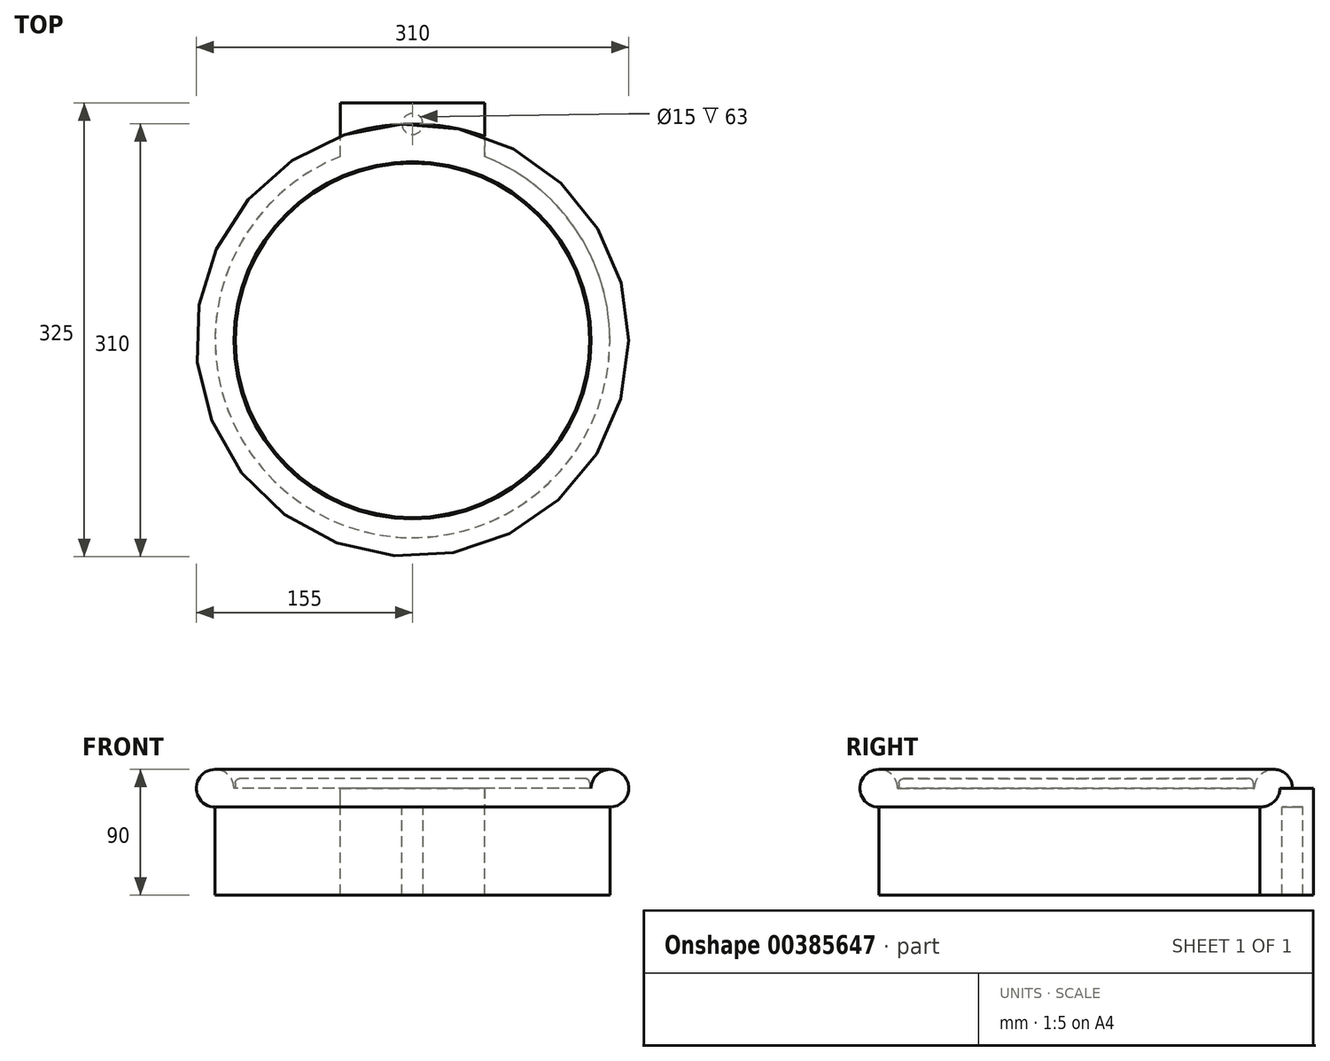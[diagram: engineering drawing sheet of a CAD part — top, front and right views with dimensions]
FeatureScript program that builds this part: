
annotation { "Feature Type Name" : "Feature", "Feature Type Description" : "" }
export const myFeature = defineFeature(function(context is Context, id is Id, definition is map)
    precondition{}
    {
        {
            var Q0;
            Q0=qCreatedBy(makeId("Top.planeOp"),FACE);
            var sketch = newSketch(context, id + "F0", { "sketchPlane" : qUnion([Q0])});
            skCircle(sketch, "E0", {"center": v(0, 0) * mm, "radius": 155 * mm});
            skCircle(sketch, "E1", {"center": v(0, 0) * mm, "radius": 141.5 * mm});
            skCircle(sketch, "E2", {"center": v(0, 0) * mm, "radius": 128 * mm});
            skCircle(sketch, "E3", {"center": v(0, 0) * mm, "radius": 127 * mm});
            skLineSegment(sketch, "E4.top", {"start": v(-51.67, 170) * mm, "end": v(51.67, 170) * mm});
            skLineSegment(sketch, "E4.left", {"start": v(-51.67, 131.73) * mm, "end": v(-51.67, 170) * mm});
            skLineSegment(sketch, "E4.right", {"start": v(51.67, 131.73) * mm, "end": v(51.67, 170) * mm});
            skLineSegment(sketch, "E5", {"start": v(0, 0) * mm, "end": v(0, -155) * mm, "construction": true});
            skLineSegment(sketch, "E6", {"start": v(0, -128) * mm, "end": v(0, -141.5) * mm, "construction": true});
            skLineSegment(sketch, "E7", {"start": v(-6.7, -141.5) * mm, "end": v(6.7, -141.5) * mm, "construction": true});
            skCircle(sketch, "E8", {"center": v(0, 155) * mm, "radius": 7.5 * mm});
            skSolve(sketch);
        }
        {
            assignVariable(context, id + "F1", {"name" : "raio", "anyValue" : 13.5});
        }
        {
            assignVariable(context, id + "F2", {"name" : "alt", "anyValue" : 90 - 2 * 13.5});
        }
        {
            var Q0;
            {var subQ5=sQuery(id+"F0.wireOp",EDGE,"E4.top");Q0=makeQuery(id+"F0.imprint","IMPRINT",FACE,{"disambiguationData":[TD([[makeQuery(id+"F0.imprint","IMPRINT",EDGE,{"derivedFrom":subQ5}),-1.0]])]});}
            var Q1;
            {var subQ0=sQuery(id+"F0.wireOp",EDGE,"E4.left");var subQ1=sQuery(id+"F0.wireOp",EDGE,"E0");var subQ2=makeQuery(id+"F0.imprint","INTERSECT",VERTEX,{"derivedFrom":[subQ1,subQ0]});Q1=makeQuery(id+"F0.imprint","IMPRINT",FACE,{"disambiguationData":[TD([[makeQuery(id+"F0.imprint","IMPRINT",EDGE,{"disambiguationData":[TD([[subQ2,1.0]])],"derivedFrom":subQ1}),1.0]])]});}
            var Q2;
            Q2=makeQuery(id+"F0.imprint","IMPRINT",FACE,{"disambiguationData":[TD([[makeQuery(id+"F0.imprint","IMPRINT",EDGE,{"derivedFrom":sQuery(id+"F0.wireOp",EDGE,"E2")}),-1.0]])]});
            var Q3;
            Q3=makeQuery(id+"F0.imprint","IMPRINT",FACE,{"disambiguationData":[TD([[makeQuery(id+"F0.imprint","IMPRINT",EDGE,{"derivedFrom":sQuery(id+"F0.wireOp",EDGE,"E2")}),1.0]])]});
            var Q4;
            Q4=makeQuery(id+"F0.imprint","IMPRINT",FACE,{"disambiguationData":[TD([[makeQuery(id+"F0.imprint","IMPRINT",EDGE,{"derivedFrom":sQuery(id+"F0.wireOp",EDGE,"E3")}),1.0]])]});
            extrude(context, id + "F3", {"entities" : qUnion([Q0, Q1, Q2, Q3, Q4]), "oppositeDirection" : true, "depth" : (getVariable(context, 'alt')) * mm});
        }
        {
            var Q0;
            {var subQ0=sQuery(id+"F0.wireOp",EDGE,"E4.left");var subQ1=sQuery(id+"F0.wireOp",EDGE,"E0");var subQ2=makeQuery(id+"F0.imprint","INTERSECT",VERTEX,{"derivedFrom":[subQ1,subQ0]});Q0=makeQuery(id+"F0.imprint","IMPRINT",FACE,{"disambiguationData":[TD([[makeQuery(id+"F0.imprint","IMPRINT",EDGE,{"disambiguationData":[TD([[subQ2,-1.0]])],"derivedFrom":subQ1}),1.0]])]});}
            var Q1;
            Q1=makeQuery(id+"F0.imprint","IMPRINT",FACE,{"disambiguationData":[TD([[makeQuery(id+"F0.imprint","IMPRINT",EDGE,{"derivedFrom":sQuery(id+"F0.wireOp",EDGE,"E2")}),-1.0]])]});
            var Q2;
            Q2=makeQuery(id+"F0.imprint","IMPRINT",FACE,{"disambiguationData":[TD([[makeQuery(id+"F0.imprint","IMPRINT",EDGE,{"derivedFrom":sQuery(id+"F0.wireOp",EDGE,"E2")}),1.0]])]});
            var Q3;
            Q3=makeQuery(id+"F0.imprint","IMPRINT",FACE,{"disambiguationData":[TD([[makeQuery(id+"F0.imprint","IMPRINT",EDGE,{"derivedFrom":sQuery(id+"F0.wireOp",EDGE,"E3")}),1.0]])]});
            var Q4;
            {var subQ0=sQuery(id+"F0.wireOp",EDGE,"E4.left");var subQ1=sQuery(id+"F0.wireOp",EDGE,"E0");var subQ2=makeQuery(id+"F0.imprint","INTERSECT",VERTEX,{"derivedFrom":[subQ1,subQ0]});Q4=makeQuery(id+"F0.imprint","IMPRINT",FACE,{"disambiguationData":[TD([[makeQuery(id+"F0.imprint","IMPRINT",EDGE,{"disambiguationData":[TD([[subQ2,1.0]])],"derivedFrom":subQ1}),1.0]])]});}
            var Q5;
            {var subQ5=sQuery(id+"F0.wireOp",EDGE,"E4.top");Q5=makeQuery(id+"F0.imprint","IMPRINT",FACE,{"disambiguationData":[TD([[makeQuery(id+"F0.imprint","IMPRINT",EDGE,{"derivedFrom":subQ5}),-1.0]])]});}
            var Q6;
            {var subQ0=sQuery(id+"F0.wireOp",EDGE,"E8");var subQ1=sQuery(id+"F0.wireOp",EDGE,"E0");var subQ2=makeQuery(id+"F0.imprint","INTERSECT",VERTEX,{"disambiguationData":[OD(0.0)],"derivedFrom":[subQ1,subQ0]});Q6=makeQuery(id+"F0.imprint","IMPRINT",FACE,{"disambiguationData":[TD([[makeQuery(id+"F0.imprint","IMPRINT",EDGE,{"disambiguationData":[TD([[subQ2,-1.0]])],"derivedFrom":subQ1}),1.0]])]});}
            var Q7;
            {var subQ0=sQuery(id+"F0.wireOp",EDGE,"E8");var subQ1=sQuery(id+"F0.wireOp",EDGE,"E0");var subQ2=makeQuery(id+"F0.imprint","INTERSECT",VERTEX,{"disambiguationData":[OD(0.0)],"derivedFrom":[subQ1,subQ0]});Q7=makeQuery(id+"F0.imprint","IMPRINT",FACE,{"disambiguationData":[TD([[makeQuery(id+"F0.imprint","IMPRINT",EDGE,{"disambiguationData":[TD([[subQ2,-1.0]])],"derivedFrom":subQ1}),-1.0]])]});}
            extrude(context, id + "F4", {"entities" : qUnion([Q0, Q1, Q2, Q3, Q4, Q5, Q6, Q7]), "operationType" : NewBodyOperationType.ADD, "depth" : (getVariable(context, 'raio')) * mm});
        }
        {
            var Q0;
            {var subQ0=sQuery(id+"F0.wireOp",EDGE,"E4.left");var subQ1=sQuery(id+"F0.wireOp",EDGE,"E0");var subQ2=makeQuery(id+"F0.imprint","INTERSECT",VERTEX,{"derivedFrom":[subQ1,subQ0]});Q0=makeQuery(id+"F0.imprint","IMPRINT",FACE,{"disambiguationData":[TD([[makeQuery(id+"F0.imprint","IMPRINT",EDGE,{"disambiguationData":[TD([[subQ2,-1.0]])],"derivedFrom":subQ1}),1.0]])]});}
            var Q1;
            Q1=makeQuery(id+"F0.imprint","IMPRINT",FACE,{"disambiguationData":[TD([[makeQuery(id+"F0.imprint","IMPRINT",EDGE,{"derivedFrom":sQuery(id+"F0.wireOp",EDGE,"E2")}),-1.0]])]});
            var Q2;
            {var subQ0=sQuery(id+"F0.wireOp",EDGE,"E4.left");var subQ1=sQuery(id+"F0.wireOp",EDGE,"E0");var subQ2=makeQuery(id+"F0.imprint","INTERSECT",VERTEX,{"derivedFrom":[subQ1,subQ0]});Q2=makeQuery(id+"F0.imprint","IMPRINT",FACE,{"disambiguationData":[TD([[makeQuery(id+"F0.imprint","IMPRINT",EDGE,{"disambiguationData":[TD([[subQ2,1.0]])],"derivedFrom":subQ1}),1.0]])]});}
            var Q3;
            {var subQ0=sQuery(id+"F0.wireOp",EDGE,"E8");var subQ1=sQuery(id+"F0.wireOp",EDGE,"E0");var subQ2=makeQuery(id+"F0.imprint","INTERSECT",VERTEX,{"disambiguationData":[OD(0.0)],"derivedFrom":[subQ1,subQ0]});Q3=makeQuery(id+"F0.imprint","IMPRINT",FACE,{"disambiguationData":[TD([[makeQuery(id+"F0.imprint","IMPRINT",EDGE,{"disambiguationData":[TD([[subQ2,-1.0]])],"derivedFrom":subQ1}),1.0]])]});}
            extrude(context, id + "F5", {"entities" : qUnion([Q0, Q1, Q2, Q3]), "operationType" : NewBodyOperationType.ADD, "depth" : (2 * getVariable(context, 'raio')) * mm, "hasSecondDirection" : true, "secondDirectionOppositeDirection" : false, "secondDirectionDepth" : (getVariable(context, 'raio')) * mm});
        }
        {
            var Q0;
            Q0=makeQuery(id+"F5.opExtrude","CAP_EDGE",EDGE,{"disambiguationData":[OSD([sQuery(id+"F0.wireOp",EDGE,"E0")])],"isStart":false});
            var Q1;
            Q1=makeQuery(id+"F5.opExtrude","CAP_EDGE",EDGE,{"disambiguationData":[OSD([sQuery(id+"F0.wireOp",EDGE,"E2")])],"isStart":false});
            var Q2;
            Q2=makeQuery(id+"F4.opExtrude","CAP_EDGE",EDGE,{"disambiguationData":[OSD([sQuery(id+"F0.wireOp",EDGE,"E0")])],"isStart":true});
            fillet(context, id + "F6", {"entities" : qUnion([Q0, Q1, Q2]), "radius" : (getVariable(context, 'raio')) * mm, "tangentPropagation" : true, "allowEdgeOverflow" : false});
        }
        {
            var Q0;
            Q0=makeQuery(id+"F0.imprint","IMPRINT",FACE,{"disambiguationData":[TD([[makeQuery(id+"F0.imprint","IMPRINT",EDGE,{"derivedFrom":sQuery(id+"F0.wireOp",EDGE,"E3")}),1.0]])]});
            extrude(context, id + "F7", {"entities" : qUnion([Q0]), "depth" : 1.5 * (getVariable(context, 'raio')) * mm, "hasSecondDirection" : true, "secondDirectionOppositeDirection" : false, "secondDirectionDepth" : (getVariable(context, 'raio')) * mm});
        }
        {
            var Q0;
            Q0=makeQuery(id+"F7.opExtrude","CAP_EDGE",EDGE,{"disambiguationData":[OSD([sQuery(id+"F0.wireOp",EDGE,"E3")])],"isStart":false});
            fillet(context, id + "F8", {"entities" : qUnion([Q0]), "radius" : 3 * mm, "tangentPropagation" : true, "allowEdgeOverflow" : false});
        }
    });
